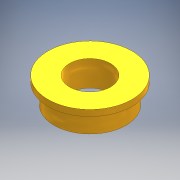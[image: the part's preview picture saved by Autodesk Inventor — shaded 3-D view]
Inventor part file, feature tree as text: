
AUTODESK INVENTOR PART (.ipt)
format: ipt  version: 2020.2 (Build 242310000, 310)  size: 106,496 bytes
history: native  units: mm
features: extrude x2, other x1, sketch x1
ambient origin geometry x8: Origin, YZ Plane, XZ Plane, XY Plane, X Axis, Y Axis, Z Axis, Center Point
bodies: Body1 (feature_tree)
feature tree (4):
  other  "ソリッド1"
  sketch  "スケッチ1"
  extrude  "押し出し1"  Depth=4.0mm
  extrude  "押し出し2"  Depth=7.0mm
